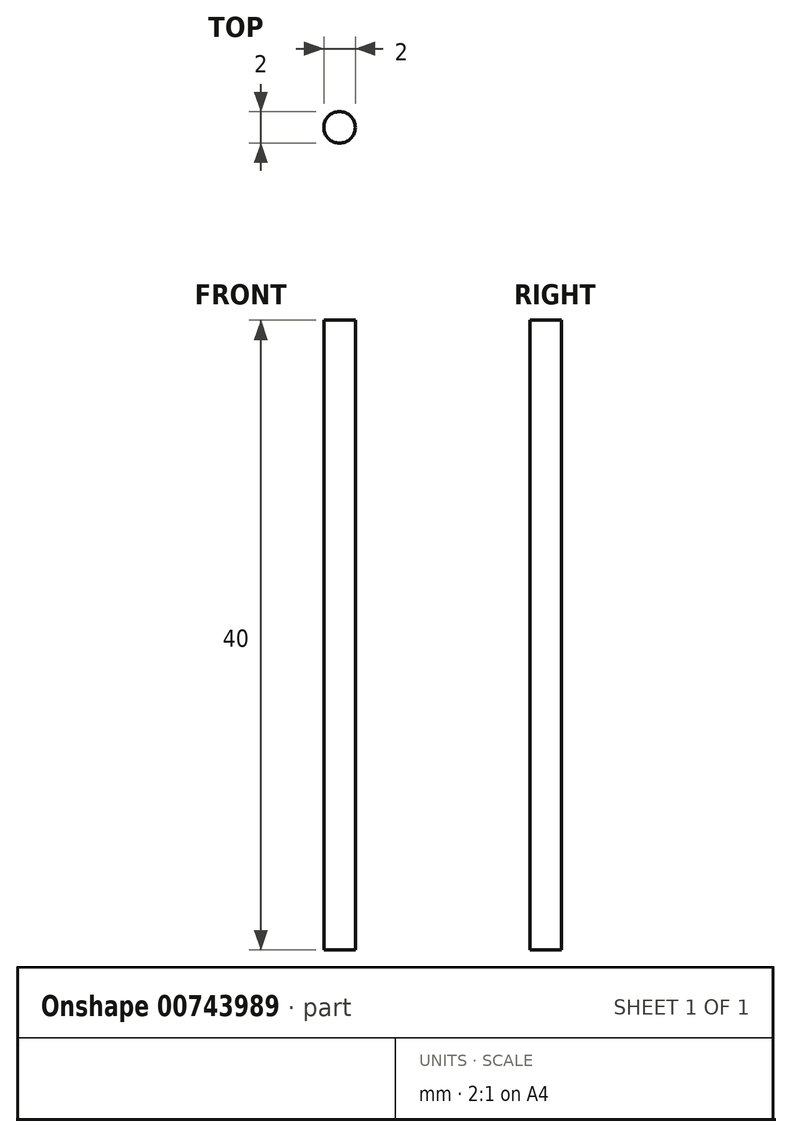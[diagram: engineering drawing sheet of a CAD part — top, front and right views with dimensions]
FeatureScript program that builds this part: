
annotation { "Feature Type Name" : "Feature", "Feature Type Description" : "" }
export const myFeature = defineFeature(function(context is Context, id is Id, definition is map)
    precondition{}
    {
        {
            var Q0;
            Q0=qCreatedBy(makeId("Top.planeOp"),FACE);
            var sketch = newSketch(context, id + "F0", { "sketchPlane" : qUnion([Q0])});
            skCircle(sketch, "E0", {"center": v(0, 0) * mm, "radius": 1 * mm});
            skSolve(sketch);
        }
        {
            var Q0;
            Q0=makeQuery(id+"F0.imprint","IMPRINT",FACE,{"disambiguationData":[TD([[makeQuery(id+"F0.imprint","IMPRINT",EDGE,{"derivedFrom":sQuery(id+"F0.wireOp",EDGE,"E0")}),1.0]])]});
            extrude(context, id + "F1", {"entities" : qUnion([Q0]), "depth" : 40 * mm, "offsetDistance" : 25 * mm});
        }
    });
